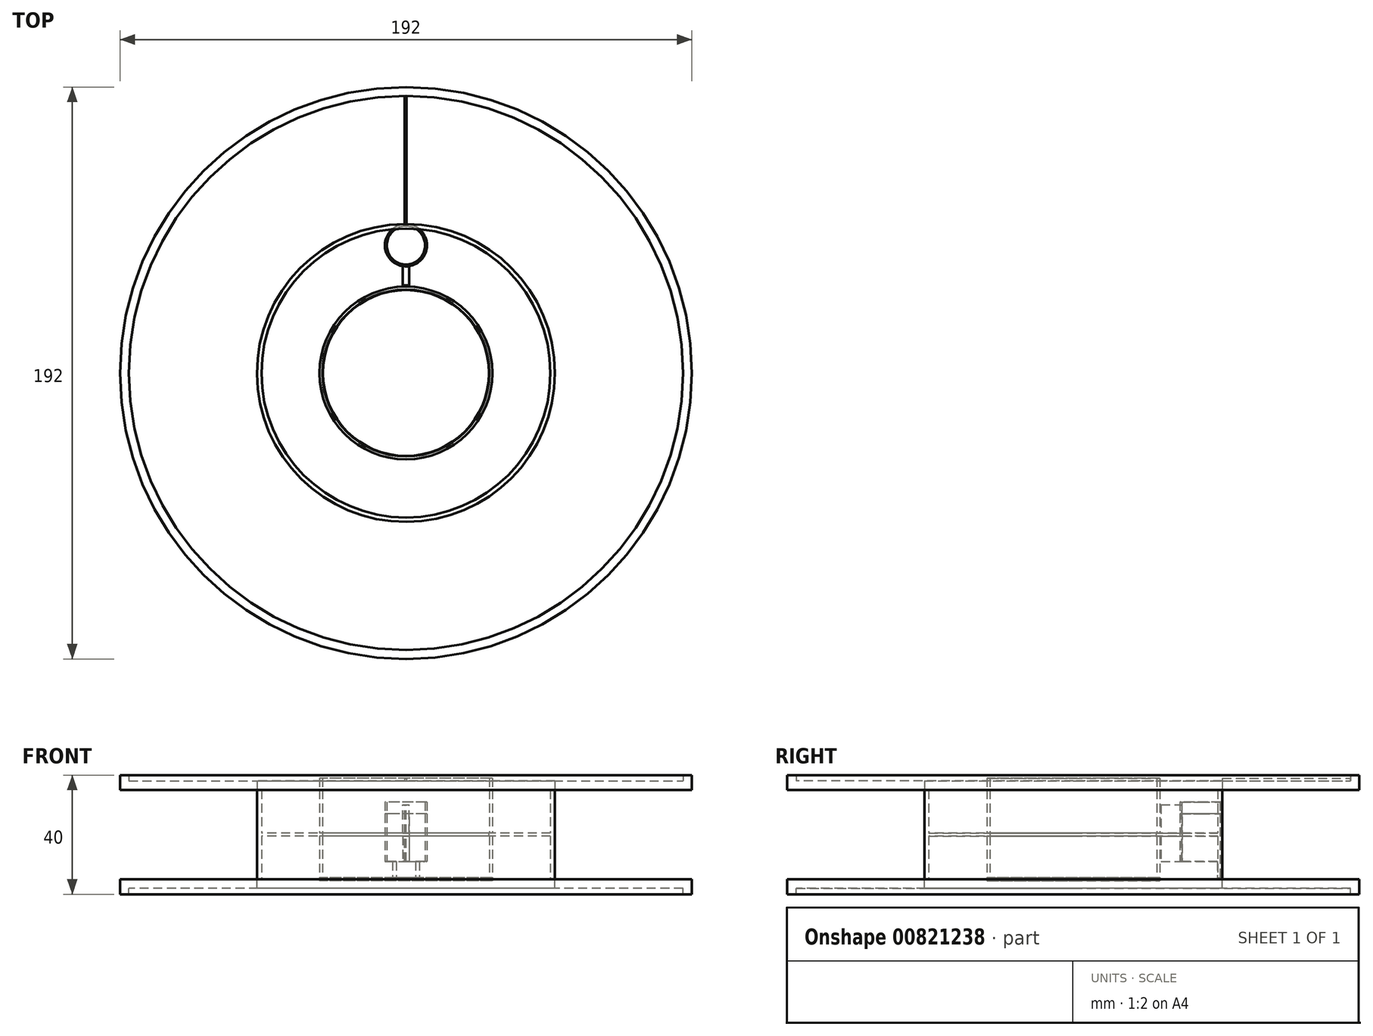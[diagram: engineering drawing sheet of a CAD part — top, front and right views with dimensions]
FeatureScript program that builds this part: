
annotation { "Feature Type Name" : "Feature", "Feature Type Description" : "" }
export const myFeature = defineFeature(function(context is Context, id is Id, definition is map)
    precondition{}
    {
        {
            var Q0;
            Q0=qCreatedBy(makeId("Top.planeOp"),FACE);
            var sketch = newSketch(context, id + "F0", { "sketchPlane" : qUnion([Q0])});
            skCircle(sketch, "E0", {"center": v(0, 0) * mm, "radius": 28 * mm});
            skCircle(sketch, "E1", {"center": v(0, 0) * mm, "radius": 93 * mm});
            skCircle(sketch, "E2", {"center": v(0, 0) * mm, "radius": 48.5 * mm});
            skCircle(sketch, "E3", {"center": v(0, 0) * mm, "radius": 29 * mm});
            skCircle(sketch, "E4", {"center": v(0, 0) * mm, "radius": 96 * mm});
            skCircle(sketch, "E5", {"center": v(0, 0) * mm, "radius": 50 * mm});
            skSolve(sketch);
        }
        {
            var Q0;
            Q0=makeQuery(id+"F0.imprint","IMPRINT",FACE,{"disambiguationData":[TD([[makeQuery(id+"F0.imprint","IMPRINT",EDGE,{"derivedFrom":sQuery(id+"F0.wireOp",EDGE,"E0")}),-1.0]])]});
            var Q1;
            Q1=makeQuery(id+"F0.imprint","IMPRINT",FACE,{"disambiguationData":[TD([[makeQuery(id+"F0.imprint","IMPRINT",EDGE,{"derivedFrom":sQuery(id+"F0.wireOp",EDGE,"E2")}),-1.0]])]});
            extrude(context, id + "F1", {"entities" : qUnion([Q0, Q1]), "depth" : 30 * mm, "offsetDistance" : 25 * mm});
        }
        {
            var Q0;
            Q0=makeQuery(id+"F0.imprint","IMPRINT",FACE,{"disambiguationData":[TD([[makeQuery(id+"F0.imprint","IMPRINT",EDGE,{"derivedFrom":sQuery(id+"F0.wireOp",EDGE,"E2")}),1.0]])]});
            extrude(context, id + "F2", {"entities" : qUnion([Q0]), "depth" : .5 * mm, "offsetDistance" : 25 * mm});
        }
        {
            var Q0;
            Q0=makeQuery(id+"F0.imprint","IMPRINT",FACE,{"disambiguationData":[TD([[makeQuery(id+"F0.imprint","IMPRINT",EDGE,{"derivedFrom":sQuery(id+"F0.wireOp",EDGE,"E1")}),-1.0]])]});
            extrude(context, id + "F3", {"entities" : qUnion([Q0]), "oppositeDirection" : true, "depth" : 5 * mm, "offsetDistance" : 25 * mm});
        }
        {
            var Q0;
            Q0=makeQuery(id+"F0.imprint","IMPRINT",FACE,{"disambiguationData":[TD([[makeQuery(id+"F0.imprint","IMPRINT",EDGE,{"derivedFrom":sQuery(id+"F0.wireOp",EDGE,"E1")}),1.0]])]});
            extrude(context, id + "F4", {"entities" : qUnion([Q0]), "oppositeDirection" : true, "depth" : 3 * mm, "offsetDistance" : 25 * mm});
        }
        {
            var Q0;
            Q0=makeQuery(id+"F0.imprint","IMPRINT",FACE,{"disambiguationData":[TD([[makeQuery(id+"F0.imprint","IMPRINT",EDGE,{"derivedFrom":sQuery(id+"F0.wireOp",EDGE,"E0")}),-1.0]])]});
            extrude(context, id + "F5", {"entities" : qUnion([Q0]), "depth" : 1 * mm, "offsetDistance" : 25 * mm, "symmetric" : true});
        }
        {
            var Q0;
            Q0=qCreatedBy(makeId("Top.planeOp"),FACE);
            var sketch = newSketch(context, id + "F6", { "sketchPlane" : qUnion([Q0])});
            skLineSegment(sketch, "E6.bottom", {"start": v(-1.12, 29.46) * mm, "end": v(1.1, 29.46) * mm});
            skLineSegment(sketch, "E6.top", {"start": v(-1.12, 48.1) * mm, "end": v(1.1, 48.1) * mm});
            skLineSegment(sketch, "E6.left", {"start": v(-1.12, 29.46) * mm, "end": v(-1.12, 48.1) * mm});
            skLineSegment(sketch, "E6.right", {"start": v(1.1, 29.46) * mm, "end": v(1.1, 48.1) * mm});
            skSolve(sketch);
        }
        {
            var Q0;
            Q0 = qSketchRegion(id + "F6", true);
            extrude(context, id + "F7", {"entities" : qUnion([Q0]), "operationType" : NewBodyOperationType.ADD, "depth" : 21 * mm, "offsetDistance" : 25 * mm});
        }
        {
            var Q0;
            Q0=makeQuery(id+"F7.opExtrude","CAP_FACE",FACE,{"disambiguationData":[OSD([sQuery(id+"F6.wireOp",EDGE,"E6.bottom"),sQuery(id+"F6.wireOp",EDGE,"E6.top"),sQuery(id+"F6.wireOp",EDGE,"E6.left"),sQuery(id+"F6.wireOp",EDGE,"E6.right")])],"isStart":false});
            var sketch = newSketch(context, id + "F8", { "sketchPlane" : qUnion([Q0])});
            skCircle(sketch, "E7", {"center": v(0, 42.86) * mm, "radius": 7.06 * mm});
            skCircle(sketch, "E8", {"center": v(0, 42.86) * mm, "radius": 6.42 * mm});
            skSolve(sketch);
        }
        {
            var Q0;
            {var subQ0=sQuery(id+"F8.wireOp",EDGE,"E7");var subQ1=makeQuery(id+"F7.opExtrude","CAP_EDGE",EDGE,{"disambiguationData":[OSD([sQuery(id+"F6.wireOp",EDGE,"E6.left")])],"isStart":false});var subQ2=makeQuery(id+"F8.imprint","INTERSECT",VERTEX,{"derivedFrom":[subQ1,subQ0]});Q0=makeQuery(id+"F8.imprint","IMPRINT",FACE,{"disambiguationData":[TD([[makeQuery(id+"F8.imprint","IMPRINT",EDGE,{"disambiguationData":[TD([[subQ2,1.0]])],"derivedFrom":subQ0}),1.0]])]});}
            var Q1;
            {var subQ0=sQuery(id+"F8.wireOp",EDGE,"E7");var subQ1=makeQuery(id+"F7.opExtrude","CAP_EDGE",EDGE,{"disambiguationData":[OSD([sQuery(id+"F6.wireOp",EDGE,"E6.left")])],"isStart":false});var subQ2=makeQuery(id+"F8.imprint","INTERSECT",VERTEX,{"derivedFrom":[subQ1,subQ0]});Q1=makeQuery(id+"F8.imprint","IMPRINT",FACE,{"disambiguationData":[TD([[makeQuery(id+"F8.imprint","IMPRINT",EDGE,{"disambiguationData":[TD([[subQ2,-1.0]])],"derivedFrom":subQ0}),1.0]])]});}
            extrude(context, id + "F9", {"entities" : qUnion([Q0, Q1]), "depth" : 1 * mm, "offsetDistance" : 25 * mm, "hasSecondDirection" : true, "secondDirectionOppositeDirection" : true, "secondDirectionDepth" : 20.5 * mm});
        }
        {
            var Q0;
            Q0=makeQuery(id+"F7.opExtrude","CAP_FACE",FACE,{"disambiguationData":[OSD([sQuery(id+"F6.wireOp",EDGE,"E6.bottom"),sQuery(id+"F6.wireOp",EDGE,"E6.top"),sQuery(id+"F6.wireOp",EDGE,"E6.left"),sQuery(id+"F6.wireOp",EDGE,"E6.right")])],"isStart":false});
            var sketch = newSketch(context, id + "F10", { "sketchPlane" : qUnion([Q0])});
            skLineSegment(sketch, "E9", {"start": v(-1.12, 36.54) * mm, "end": v(-0.43, 36.47) * mm});
            skLineSegment(sketch, "E10", {"start": v(-0.43, 36.47) * mm, "end": v(0.07, 36.47) * mm});
            skLineSegment(sketch, "E11", {"start": v(0.07, 36.47) * mm, "end": v(1.1, 36.53) * mm});
            skSolve(sketch);
        }
        {
            var Q0;
            {var subQ2=sQuery(id+"F10.wireOp",EDGE,"E9");Q0=makeQuery(id+"F10.imprint","IMPRINT",FACE,{"disambiguationData":[TD([[makeQuery(id+"F10.imprint","IMPRINT",EDGE,{"derivedFrom":subQ2}),1.0]])]});}
            extrude(context, id + "F11", {"entities" : qUnion([Q0]), "operationType" : NewBodyOperationType.REMOVE, "oppositeDirection" : true, "depth" : 20.5 * mm, "offsetDistance" : 25 * mm});
        }
        {
            var Q0;
            Q0=makeQuery(id+"F1.opExtrude","CAP_FACE",FACE,{"disambiguationData":[OSD([sQuery(id+"F0.wireOp",EDGE,"E2"),sQuery(id+"F0.wireOp",EDGE,"E5")])],"isStart":false});
            var sketch = newSketch(context, id + "F12", { "sketchPlane" : qUnion([Q0])});
            skLineSegment(sketch, "E12", {"start": v(-21.44, 43.5) * mm, "end": v(-23.01, 53.91) * mm});
            skSolve(sketch);
        }
        {
            var Q0;
            Q0=qCreatedBy(makeId("Top.planeOp"),FACE);
            cPlane(context, id + "F13", {"entities" : qUnion([Q0]), "cplaneType" : CPlaneType.OFFSET, "offset" : 15 * mm, "width" : 150 * mm, "height" : 150 * mm});
        }
        {
            var Q0;
            Q0=makeQuery(id+"F4.opExtrude","SWEPT_BODY",BODY,{"disambiguationData":[OSD([sQuery(id+"F0.wireOp",EDGE,"E1"),sQuery(id+"F0.wireOp",EDGE,"E5")])]});
            var Q1;
            Q1=makeQuery(id+"F3.opExtrude","SWEPT_BODY",BODY,{"disambiguationData":[OSD([sQuery(id+"F0.wireOp",EDGE,"E1"),sQuery(id+"F0.wireOp",EDGE,"E4")])]});
            var Q2;
            Q2=qCreatedBy(id+"F13.planeOp",FACE);
            mirror(context, id + "F14", {"entities" : qUnion([Q0, Q1]), "mirrorPlane" : qUnion([Q2])});
        }
        {
            var Q0;
            Q0=makeQuery(id+"F0.imprint","IMPRINT",FACE,{"disambiguationData":[TD([[makeQuery(id+"F0.imprint","IMPRINT",EDGE,{"derivedFrom":sQuery(id+"F0.wireOp",EDGE,"E2")}),1.0]])]});
            extrude(context, id + "F15", {"entities" : qUnion([Q0]), "operationType" : NewBodyOperationType.REMOVE, "depth" : 6 * mm, "offsetDistance" : 25 * mm});
        }
        {
            var Q0;
            Q0=qCreatedBy(id+"F13.planeOp",FACE);
            var sketch = newSketch(context, id + "F16", { "sketchPlane" : qUnion([Q0])});
            skCircle(sketch, "E13", {"center": v(0, 0) * mm, "radius": 49.25 * mm});
            skSolve(sketch);
        }
        {
            var Q0;
            Q0 = qSketchRegion(id + "F16", true);
            extrude(context, id + "F17", {"entities" : qUnion([Q0]), "depth" : 1 * mm, "offsetDistance" : 25 * mm, "symmetric" : true});
        }
        {
            var Q0;
            Q0=makeQuery(id+"F12.imprint","IMPRINT",FACE,{"disambiguationData":[TD([[makeQuery(id+"F12.imprint","IMPRINT",EDGE,{"derivedFrom":makeQuery(id+"F1.opExtrude","CAP_EDGE",EDGE,{"disambiguationData":[OSD([sQuery(id+"F0.wireOp",EDGE,"E2")])],"isStart":false})}),1.0]])]});
            var sketch = newSketch(context, id + "F18", { "sketchPlane" : qUnion([Q0])});
            skCircle(sketch, "E14", {"center": v(0, 0) * mm, "radius": 27.85 * mm});
            skSolve(sketch);
        }
        {
            var Q0;
            Q0 = qSketchRegion(id + "F18", true);
            extrude(context, id + "F19", {"entities" : qUnion([Q0]), "operationType" : NewBodyOperationType.REMOVE, "oppositeDirection" : true, "depth" : 25 * mm, "offsetDistance" : 25 * mm});
        }
        {
            var Q0;
            Q0=makeQuery(id+"F14.opPattern","COPY",FACE,{"derivedFrom":makeQuery(id+"F4.opExtrude","CAP_FACE",FACE,{"disambiguationData":[OSD([sQuery(id+"F0.wireOp",EDGE,"E1"),sQuery(id+"F0.wireOp",EDGE,"E5")])],"isStart":false}),"instanceName":"1"});
            var sketch = newSketch(context, id + "F20", { "sketchPlane" : qUnion([Q0])});
            skLineSegment(sketch, "E15.bottom", {"start": v(-0.39, 50) * mm, "end": v(0.2, 50) * mm});
            skLineSegment(sketch, "E15.top", {"start": v(-0.39, 92.89) * mm, "end": v(0.2, 92.89) * mm});
            skLineSegment(sketch, "E15.left", {"start": v(-0.39, 50) * mm, "end": v(-0.39, 92.89) * mm});
            skLineSegment(sketch, "E15.right", {"start": v(0.2, 50) * mm, "end": v(0.2, 92.89) * mm});
            skSolve(sketch);
        }
        {
            var Q0;
            Q0 = qSketchRegion(id + "F20", true);
            extrude(context, id + "F21", {"entities" : qUnion([Q0]), "operationType" : NewBodyOperationType.ADD, "depth" : 1 * mm, "offsetDistance" : 25 * mm});
        }
        {
            var Q0;
            Q0=makeQuery(id+"FSTisreExkUNbMB_6.1.F7.opExtrude","CAP_FACE",FACE,{"disambiguationData":[OSD([sQuery(id+"F6.wireOp",EDGE,"E6.bottom"),sQuery(id+"F6.wireOp",EDGE,"E6.top"),sQuery(id+"F6.wireOp",EDGE,"E6.left"),sQuery(id+"F6.wireOp",EDGE,"E6.right")])],"isStart":false});
            var Q1;
            Q1=makeQuery(id+"FSTisreExkUNbMB_6.2.F7.opExtrude","CAP_FACE",FACE,{"disambiguationData":[OSD([sQuery(id+"F6.wireOp",EDGE,"E6.bottom"),sQuery(id+"F6.wireOp",EDGE,"E6.top"),sQuery(id+"F6.wireOp",EDGE,"E6.left"),sQuery(id+"F6.wireOp",EDGE,"E6.right")])],"isStart":false});
            var Q2;
            Q2=makeQuery(id+"F9.opExtrude","CAP_FACE",FACE,{"disambiguationData":[OSD([sQuery(id+"F8.wireOp",EDGE,"E7"),sQuery(id+"F8.wireOp",EDGE,"E8")])],"isStart":false});
            var Q3;
            Q3=makeQuery(id+"F7.opExtrude","CAP_FACE",FACE,{"disambiguationData":[OSD([sQuery(id+"F6.wireOp",EDGE,"E6.bottom"),sQuery(id+"F6.wireOp",EDGE,"E6.top"),sQuery(id+"F6.wireOp",EDGE,"E6.left"),sQuery(id+"F6.wireOp",EDGE,"E6.right")])],"isStart":false});
            var Q4;
            Q4=makeQuery(id+"FSTisreExkUNbMB_6.5.F7.opExtrude","CAP_FACE",FACE,{"disambiguationData":[OSD([sQuery(id+"F6.wireOp",EDGE,"E6.bottom"),sQuery(id+"F6.wireOp",EDGE,"E6.top"),sQuery(id+"F6.wireOp",EDGE,"E6.left"),sQuery(id+"F6.wireOp",EDGE,"E6.right")])],"isStart":false});
            var Q5;
            Q5=makeQuery(id+"FSTisreExkUNbMB_6.3.F7.opExtrude","CAP_FACE",FACE,{"disambiguationData":[OSD([sQuery(id+"F6.wireOp",EDGE,"E6.bottom"),sQuery(id+"F6.wireOp",EDGE,"E6.top"),sQuery(id+"F6.wireOp",EDGE,"E6.left"),sQuery(id+"F6.wireOp",EDGE,"E6.right")])],"isStart":false});
            var Q6;
            Q6=makeQuery(id+"FSTisreExkUNbMB_6.4.F7.opExtrude","CAP_FACE",FACE,{"disambiguationData":[OSD([sQuery(id+"F6.wireOp",EDGE,"E6.bottom"),sQuery(id+"F6.wireOp",EDGE,"E6.top"),sQuery(id+"F6.wireOp",EDGE,"E6.left"),sQuery(id+"F6.wireOp",EDGE,"E6.right")])],"isStart":false});
            var Q7;
            Q7=makeQuery(id+"F1.opExtrude","CAP_FACE",FACE,{"disambiguationData":[OSD([sQuery(id+"F0.wireOp",EDGE,"E0"),sQuery(id+"F0.wireOp",EDGE,"E3")])],"isStart":false});
            extrude(context, id + "F22", {"entities" : qUnion([Q0, Q1, Q2, Q3, Q4, Q5, Q6, Q7]), "depth" : 4 * mm, "offsetDistance" : 25 * mm});
        }
        {
            var Q0;
            Q0=makeQuery(id+"F1.opExtrude","SWEPT_BODY",BODY,{"disambiguationData":[OSD([sQuery(id+"F0.wireOp",EDGE,"E0"),sQuery(id+"F0.wireOp",EDGE,"E3")])]});
            var Q1;
            Q1=makeQuery(id+"F1.opExtrude","SWEPT_BODY",BODY,{"disambiguationData":[OSD([sQuery(id+"F0.wireOp",EDGE,"E2"),sQuery(id+"F0.wireOp",EDGE,"E5")])]});
            var Q2;
            Q2=makeQuery(id+"F3.opExtrude","SWEPT_BODY",BODY,{"disambiguationData":[OSD([sQuery(id+"F0.wireOp",EDGE,"E1"),sQuery(id+"F0.wireOp",EDGE,"E4")])]});
            var Q3;
            Q3=makeQuery(id+"F4.opExtrude","SWEPT_BODY",BODY,{"disambiguationData":[OSD([sQuery(id+"F0.wireOp",EDGE,"E1"),sQuery(id+"F0.wireOp",EDGE,"E5")])]});
            var Q4;
            Q4=makeQuery(id+"F14.opPattern","COPY",BODY,{"derivedFrom":makeQuery(id+"F3.opExtrude","SWEPT_BODY",BODY,{"disambiguationData":[OSD([sQuery(id+"F0.wireOp",EDGE,"E1"),sQuery(id+"F0.wireOp",EDGE,"E4")])]}),"instanceName":"1"});
            var Q5;
            Q5=makeQuery(id+"F14.opPattern","COPY",BODY,{"derivedFrom":makeQuery(id+"F4.opExtrude","SWEPT_BODY",BODY,{"disambiguationData":[OSD([sQuery(id+"F0.wireOp",EDGE,"E1"),sQuery(id+"F0.wireOp",EDGE,"E5")])]}),"instanceName":"1"});
            var Q6;
            Q6=makeQuery(id+"F15.boolean.opBoolean","SPLIT",BODY,{"disambiguationData":[OD(2.0)],"derivedFrom":makeQuery(id+"F2.opExtrude","SWEPT_BODY",BODY,{"disambiguationData":[OSD([sQuery(id+"F0.wireOp",EDGE,"E2"),sQuery(id+"F0.wireOp",EDGE,"E3")])]})});
            var Q7;
            Q7=makeQuery(id+"F15.boolean.opBoolean","SPLIT",BODY,{"disambiguationData":[OD(3.0)],"derivedFrom":makeQuery(id+"F2.opExtrude","SWEPT_BODY",BODY,{"disambiguationData":[OSD([sQuery(id+"F0.wireOp",EDGE,"E2"),sQuery(id+"F0.wireOp",EDGE,"E3")])]})});
            var Q8;
            Q8=makeQuery(id+"F15.boolean.opBoolean","SPLIT",BODY,{"disambiguationData":[OD(4.0)],"derivedFrom":makeQuery(id+"F2.opExtrude","SWEPT_BODY",BODY,{"disambiguationData":[OSD([sQuery(id+"F0.wireOp",EDGE,"E2"),sQuery(id+"F0.wireOp",EDGE,"E3")])]})});
            var Q9;
            Q9=makeQuery(id+"F15.boolean.opBoolean","SPLIT",BODY,{"disambiguationData":[OD(5.0)],"derivedFrom":makeQuery(id+"F2.opExtrude","SWEPT_BODY",BODY,{"disambiguationData":[OSD([sQuery(id+"F0.wireOp",EDGE,"E2"),sQuery(id+"F0.wireOp",EDGE,"E3")])]})});
            var Q10;
            Q10=makeQuery(id+"F17.opExtrude","SWEPT_BODY",BODY,{"disambiguationData":[OSD([sQuery(id+"F16.wireOp",EDGE,"E13")])]});
            var Q11;
            Q11=makeQuery(id+"FzLAdbVGrgOaAd3_8.1.FLxx1x9U1bjZ50P_8.7.F21.opExtrude","SWEPT_BODY",BODY,{"disambiguationData":[OSD([sQuery(id+"F20.wireOp",EDGE,"E15.bottom"),sQuery(id+"F20.wireOp",EDGE,"E15.top"),sQuery(id+"F20.wireOp",EDGE,"E15.left"),sQuery(id+"F20.wireOp",EDGE,"E15.right")])]});
            var Q12;
            Q12=makeQuery(id+"FzLAdbVGrgOaAd3_8.1.FLxx1x9U1bjZ50P_8.10.F21.opExtrude","SWEPT_BODY",BODY,{"disambiguationData":[OSD([sQuery(id+"F20.wireOp",EDGE,"E15.bottom"),sQuery(id+"F20.wireOp",EDGE,"E15.top"),sQuery(id+"F20.wireOp",EDGE,"E15.left"),sQuery(id+"F20.wireOp",EDGE,"E15.right")])]});
            var Q13;
            Q13=makeQuery(id+"FzLAdbVGrgOaAd3_8.1.FLxx1x9U1bjZ50P_8.8.F21.opExtrude","SWEPT_BODY",BODY,{"disambiguationData":[OSD([sQuery(id+"F20.wireOp",EDGE,"E15.bottom"),sQuery(id+"F20.wireOp",EDGE,"E15.top"),sQuery(id+"F20.wireOp",EDGE,"E15.left"),sQuery(id+"F20.wireOp",EDGE,"E15.right")])]});
            var Q14;
            Q14=makeQuery(id+"FzLAdbVGrgOaAd3_8.1.FLxx1x9U1bjZ50P_8.12.F21.opExtrude","SWEPT_BODY",BODY,{"disambiguationData":[OSD([sQuery(id+"F20.wireOp",EDGE,"E15.bottom"),sQuery(id+"F20.wireOp",EDGE,"E15.top"),sQuery(id+"F20.wireOp",EDGE,"E15.left"),sQuery(id+"F20.wireOp",EDGE,"E15.right")])]});
            var Q15;
            Q15=makeQuery(id+"FzLAdbVGrgOaAd3_8.1.FLxx1x9U1bjZ50P_8.14.F21.opExtrude","SWEPT_BODY",BODY,{"disambiguationData":[OSD([sQuery(id+"F20.wireOp",EDGE,"E15.bottom"),sQuery(id+"F20.wireOp",EDGE,"E15.top"),sQuery(id+"F20.wireOp",EDGE,"E15.left"),sQuery(id+"F20.wireOp",EDGE,"E15.right")])]});
            var Q16;
            Q16=makeQuery(id+"FzLAdbVGrgOaAd3_8.1.FLxx1x9U1bjZ50P_8.16.F21.opExtrude","SWEPT_BODY",BODY,{"disambiguationData":[OSD([sQuery(id+"F20.wireOp",EDGE,"E15.bottom"),sQuery(id+"F20.wireOp",EDGE,"E15.top"),sQuery(id+"F20.wireOp",EDGE,"E15.left"),sQuery(id+"F20.wireOp",EDGE,"E15.right")])]});
            var Q17;
            Q17=makeQuery(id+"FgHFLzYEEnOZPcq_9.1.F21.opExtrude","SWEPT_BODY",BODY,{"disambiguationData":[OSD([sQuery(id+"F20.wireOp",EDGE,"E15.bottom"),sQuery(id+"F20.wireOp",EDGE,"E15.top"),sQuery(id+"F20.wireOp",EDGE,"E15.left"),sQuery(id+"F20.wireOp",EDGE,"E15.right")])]});
            var Q18;
            {var subQ0=sQuery(id+"F6.wireOp",EDGE,"E6.right");var subQ1=sQuery(id+"F6.wireOp",EDGE,"E6.left");var subQ2=sQuery(id+"F6.wireOp",EDGE,"E6.top");var subQ3=sQuery(id+"F6.wireOp",EDGE,"E6.bottom");Q18=makeQuery(id+"F22.opExtrude","SWEPT_BODY",BODY,{"disambiguationData":[OSD([subQ3,subQ2,subQ1,subQ0]),TDD([makeQuery(id+"FSTisreExkUNbMB_6.1.F7.opExtrude","CAP_FACE",FACE,{"disambiguationData":[OSD([subQ3,subQ2,subQ1,subQ0])],"isStart":false})])]});}
            var Q19;
            {var subQ0=sQuery(id+"F6.wireOp",EDGE,"E6.right");var subQ1=sQuery(id+"F6.wireOp",EDGE,"E6.left");var subQ2=sQuery(id+"F6.wireOp",EDGE,"E6.top");var subQ3=sQuery(id+"F6.wireOp",EDGE,"E6.bottom");Q19=makeQuery(id+"F22.opExtrude","SWEPT_BODY",BODY,{"disambiguationData":[OSD([subQ3,subQ2,subQ1,subQ0]),TDD([makeQuery(id+"FSTisreExkUNbMB_6.2.F7.opExtrude","CAP_FACE",FACE,{"disambiguationData":[OSD([subQ3,subQ2,subQ1,subQ0])],"isStart":false})])]});}
            var Q20;
            {var subQ0=sQuery(id+"F6.wireOp",EDGE,"E6.right");var subQ1=sQuery(id+"F6.wireOp",EDGE,"E6.left");var subQ2=sQuery(id+"F6.wireOp",EDGE,"E6.top");var subQ3=sQuery(id+"F6.wireOp",EDGE,"E6.bottom");Q20=makeQuery(id+"F22.opExtrude","SWEPT_BODY",BODY,{"disambiguationData":[OSD([subQ3,subQ2,subQ1,subQ0]),TDD([makeQuery(id+"FSTisreExkUNbMB_6.3.F7.opExtrude","CAP_FACE",FACE,{"disambiguationData":[OSD([subQ3,subQ2,subQ1,subQ0])],"isStart":false})])]});}
            var Q21;
            {var subQ0=sQuery(id+"F6.wireOp",EDGE,"E6.right");var subQ1=sQuery(id+"F6.wireOp",EDGE,"E6.left");var subQ2=sQuery(id+"F6.wireOp",EDGE,"E6.top");var subQ3=sQuery(id+"F6.wireOp",EDGE,"E6.bottom");Q21=makeQuery(id+"F22.opExtrude","SWEPT_BODY",BODY,{"disambiguationData":[OSD([subQ3,subQ2,subQ1,subQ0]),TDD([makeQuery(id+"FSTisreExkUNbMB_6.5.F7.opExtrude","CAP_FACE",FACE,{"disambiguationData":[OSD([subQ3,subQ2,subQ1,subQ0])],"isStart":false})])]});}
            var Q22;
            {var subQ0=sQuery(id+"F6.wireOp",EDGE,"E6.right");var subQ1=sQuery(id+"F6.wireOp",EDGE,"E6.left");var subQ2=sQuery(id+"F6.wireOp",EDGE,"E6.top");var subQ3=sQuery(id+"F6.wireOp",EDGE,"E6.bottom");Q22=makeQuery(id+"F22.opExtrude","SWEPT_BODY",BODY,{"disambiguationData":[OSD([subQ3,subQ2,subQ1,subQ0]),TDD([makeQuery(id+"F7.opExtrude","CAP_FACE",FACE,{"disambiguationData":[OSD([subQ3,subQ2,subQ1,subQ0])],"isStart":false})])]});}
            booleanBodies(context, id + "F23", {"operationType" : BooleanOperationType.UNION, "tools" : qUnion([Q0, Q1, Q2, Q3, Q4, Q5, Q6, Q7, Q8, Q9, Q10, Q11, Q12, Q13, Q14, Q15, Q16, Q17, Q18, Q19, Q20, Q21, Q22])});
        }
    });
